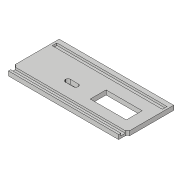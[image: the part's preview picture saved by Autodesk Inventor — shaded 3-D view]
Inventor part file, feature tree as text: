
AUTODESK INVENTOR PART (.ipt)
format: ipt  version: 2018.3 (Build 223284000, 284)  size: 157,696 bytes
history: native  units: in
note: dims shown in document units (in); Inventor stores cm internally (conversion verified against a paired STEP export)
features: extrude x6, sketch x6, fillet x3
ambient origin geometry x8: Origin, YZ Plane, XZ Plane, XY Plane, X Axis, Y Axis, Z Axis, Center Point
bodies: Solid1 (feature_tree)
feature tree (15):
  extrude  "Extrusion1"  Depth=1.5in
  extrude  "Extrusion2"  Depth=0.126in
  extrude  "Extrusion3"  Depth=0.0625in TaperAngle=0.0deg
  extrude  "Extrusion4"  Depth=0.135in
  fillet  "Fillet1"  Radius=0.0625in
  fillet  "Fillet2"  Radius=0.0625in
  extrude  "Extrusion5"  Depth=0.0625in
  fillet  "Fillet3"  Radius=0.125in
  extrude  "Extrusion6"  Depth=0.0625in TaperAngle=0.0deg
  sketch  "Sketch1"  dims[d0=3.25in d1=1.5in]
  sketch  "Sketch2"  dims[d2=0.125in d3=0.0in d6=0.126in]
  sketch  "Sketch3"  dims[d7=0.0625in d8=0.0625in d9=0.0in]
  sketch  "Sketch4"  dims[d10=0.125in d11=0.135in d12=0.0625in d13=0.0625in]
  sketch  "Sketch5"  dims[d14=0.0625in d15=0.0625in d16=0.125in]
  sketch  "Sketch6"  dims[d17=0.135in d18=0.0625in d19=0.0in d20=0.0625in d21=0.25in d22=0.25in d23=0.0625in d24=1.0in d25=0.0in d26=0.0625in d27=0.0625in d28=0.3425in d29=0.14in d30=0.36in d32=1.0in d33=0.0in d34=0.0625in d35=1.025in d36=0.45in d38=1.0in d39=0.0in d41=0.28in d43=0.25in d44=1.75in]
